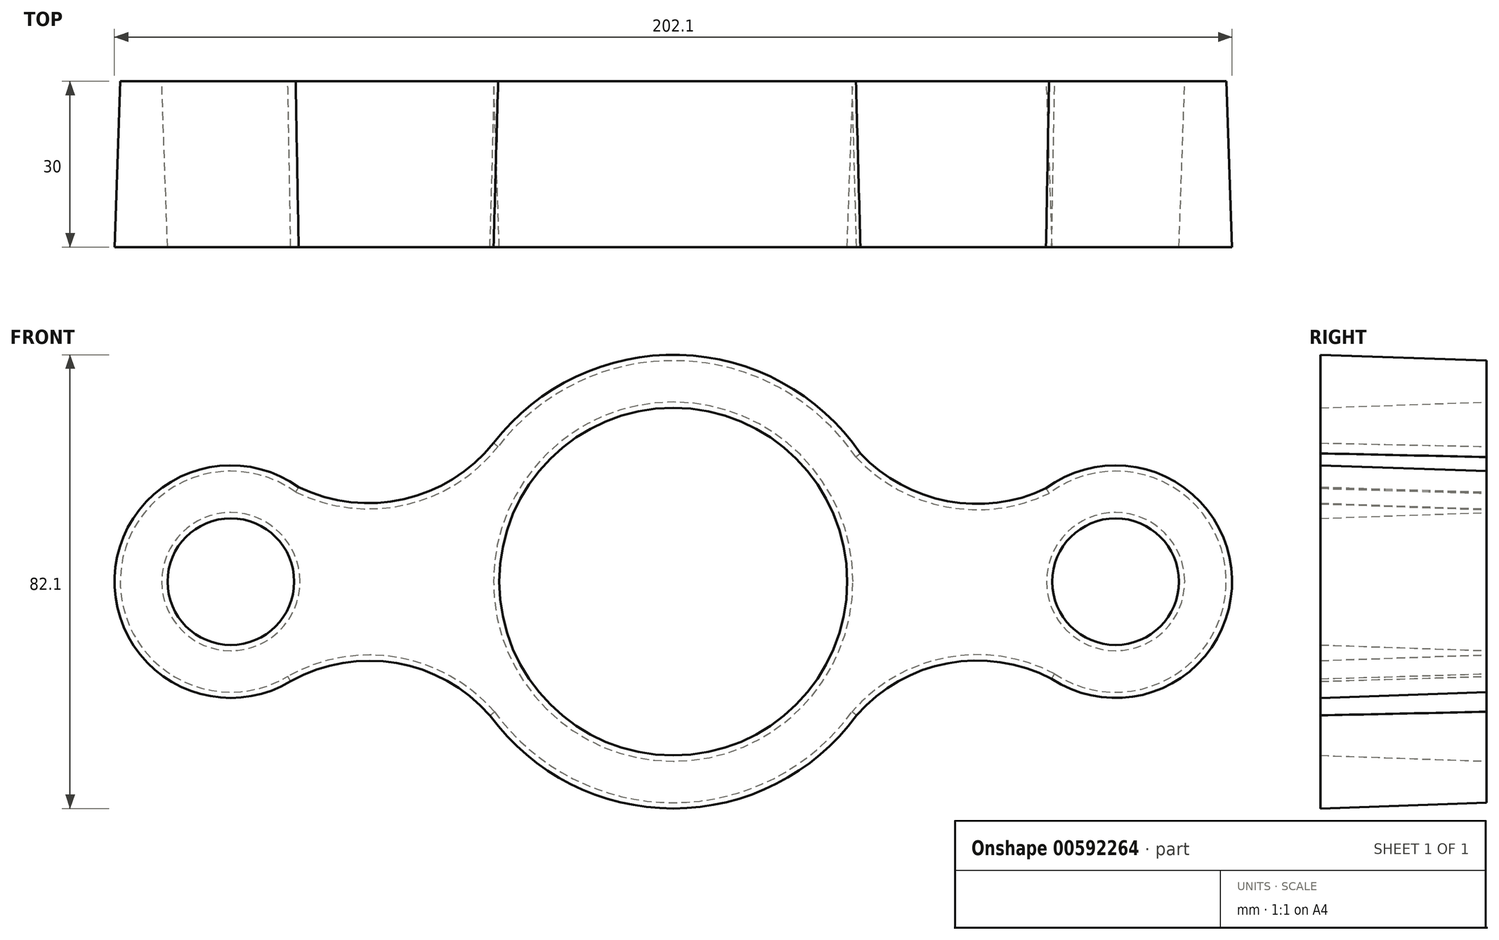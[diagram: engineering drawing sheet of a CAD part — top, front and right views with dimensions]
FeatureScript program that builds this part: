
annotation { "Feature Type Name" : "Feature", "Feature Type Description" : "" }
export const myFeature = defineFeature(function(context is Context, id is Id, definition is map)
    precondition{}
    {
        {
            var Q0;
            Q0=qCreatedBy(makeId("Front.planeOp"),FACE);
            var sketch = newSketch(context, id + "F0", { "sketchPlane" : qUnion([Q0])});
            skCircle(sketch, "E0", {"center": v(0, 0) * mm, "radius": 40 * mm});
            skCircle(sketch, "E1", {"center": v(0, 0) * mm, "radius": 32.5 * mm});
            skCircle(sketch, "E2", {"center": v(80, 0) * mm, "radius": 20 * mm});
            skCircle(sketch, "E3", {"center": v(-80, 0) * mm, "radius": 20 * mm});
            skCircle(sketch, "E4", {"center": v(-80, 0) * mm, "radius": 12.5 * mm});
            skCircle(sketch, "E5", {"center": v(80, 0) * mm, "radius": 12.5 * mm});
            skArc(sketch, "E6", {"start": v(32.61, 23.01) * mm, "mid": v(32.82, 22.78) * mm, "end": v(33.04, 22.55) * mm});
            skArc(sketch, "E7", {"start": v(33.04, 22.55) * mm, "mid": v(49.22, 13.57) * mm, "end": v(67.6, 15.8) * mm});
            skLineSegment(sketch, "E8", {"start": v(67.96, 15.97) * mm, "end": v(67.96, 15.97) * mm});
            skArc(sketch, "E9", {"start": v(67.6, 15.8) * mm, "mid": v(67.78, 15.88) * mm, "end": v(67.96, 15.97) * mm});
            skArc(sketch, "E10", {"start": v(-31.67, 24.44) * mm, "mid": v(-31.49, 24.7) * mm, "end": v(-31.31, 24.98) * mm});
            skArc(sketch, "E11", {"start": v(-68.28, 16.2) * mm, "mid": v(-48.53, 13.9) * mm, "end": v(-31.67, 24.44) * mm});
            skArc(sketch, "E12", {"start": v(-68.63, 16.45) * mm, "mid": v(-68.45, 16.33) * mm, "end": v(-68.28, 16.2) * mm});
            skArc(sketch, "E13", {"start": v(-68.95, -16.73) * mm, "mid": v(-69.14, -16.83) * mm, "end": v(-69.33, -16.94) * mm});
            skArc(sketch, "E14", {"start": v(-69.33, -16.94) * mm, "mid": v(-69.51, -17.04) * mm, "end": v(-69.7, -17.14) * mm});
            skArc(sketch, "E15", {"start": v(-32.5, -23.37) * mm, "mid": v(-32.65, -23.2) * mm, "end": v(-32.8, -23.03) * mm});
            skArc(sketch, "E16", {"start": v(-32.8, -23.03) * mm, "mid": v(-49.8, -13.71) * mm, "end": v(-68.95, -16.73) * mm});
            skArc(sketch, "E17.trimOffspring", {"start": v(-32.32, -23.57) * mm, "mid": v(-32.4, -23.47) * mm, "end": v(-32.5, -23.37) * mm});
            skArc(sketch, "E18", {"start": v(32.33, -23.55) * mm, "mid": v(31.4, -24.68) * mm, "end": v(30.52, -25.86) * mm});
            skArc(sketch, "E19", {"start": v(68.97, -16.68) * mm, "mid": v(49.46, -13.74) * mm, "end": v(32.33, -23.55) * mm});
            skArc(sketch, "E20", {"start": v(68.97, -16.68) * mm, "mid": v(48.02, -14.04) * mm, "end": v(30.52, -25.86) * mm});
            skSolve(sketch);
        }
        {
            var Q0;
            Q0 = qSketchRegion(id + "F0", true);
            extrude(context, id + "F1", {"entities" : qUnion([Q0]), "depth" : 30 * mm, "offsetDistance" : 25 * mm, "hasDraft" : true, "draftAngle" : 2 * degree});
        }
    });
